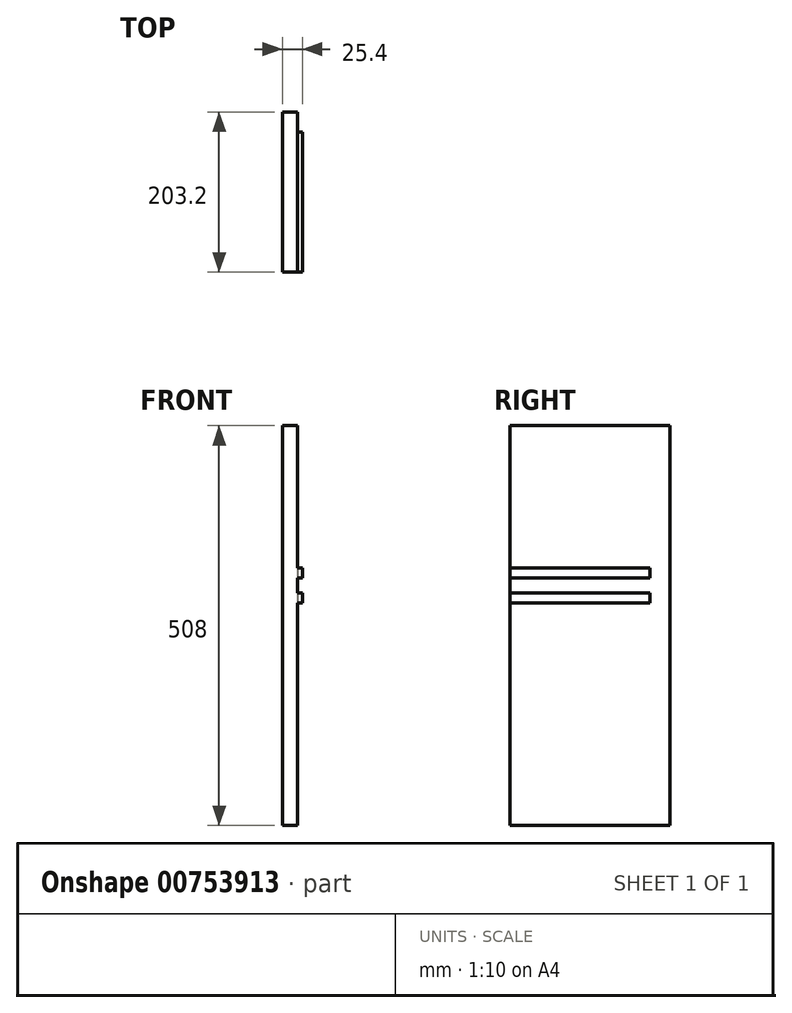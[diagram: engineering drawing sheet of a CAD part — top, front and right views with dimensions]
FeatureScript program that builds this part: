
annotation { "Feature Type Name" : "Feature", "Feature Type Description" : "" }
export const myFeature = defineFeature(function(context is Context, id is Id, definition is map)
    precondition{}
    {
        {
            var Q0;
            Q0=qCreatedBy(makeId("Right.planeOp"),FACE);
            var sketch = newSketch(context, id + "F0", { "sketchPlane" : qUnion([Q0])});
            skLineSegment(sketch, "E0.bottom", {"start": v(101.6, -254) * mm, "end": v(-101.6, -254) * mm});
            skLineSegment(sketch, "E0.top", {"start": v(101.6, 254) * mm, "end": v(-101.6, 254) * mm});
            skLineSegment(sketch, "E0.left", {"start": v(101.6, -254) * mm, "end": v(101.6, 254) * mm});
            skLineSegment(sketch, "E0.right", {"start": v(-101.6, -254) * mm, "end": v(-101.6, 254) * mm});
            skPoint(sketch, "E0.middle", {"position": v(0, 0) * mm});
            skSolve(sketch);
        }
        {
            var Q0;
            Q0=makeQuery(id+"F0.imprint","IMPRINT",FACE,{"disambiguationData":[TD([[makeQuery(id+"F0.imprint","IMPRINT",EDGE,{"derivedFrom":sQuery(id+"F0.wireOp",EDGE,"E0.bottom")}),-1.0]])]});
            extrude(context, id + "F1", {"entities" : qUnion([Q0]), "depth" : 19.05 * mm, "offsetDistance" : 25.4 * mm});
        }
        {
            var Q0;
            Q0=makeQuery(id+"F1.opExtrude","CAP_FACE",FACE,{"disambiguationData":[OSD([sQuery(id+"F0.wireOp",EDGE,"E0.bottom"),sQuery(id+"F0.wireOp",EDGE,"E0.top"),sQuery(id+"F0.wireOp",EDGE,"E0.left"),sQuery(id+"F0.wireOp",EDGE,"E0.right")])],"isStart":false});
            var sketch = newSketch(context, id + "F2", { "sketchPlane" : qUnion([Q0])});
            skLineSegment(sketch, "E1", {"start": v(0, 0) * mm, "end": v(0, 254) * mm});
            skLineSegment(sketch, "E2.bottom", {"start": v(-101.6, 73.02) * mm, "end": v(101.6, 73.02) * mm});
            skLineSegment(sketch, "E2.top", {"start": v(-101.6, 28.58) * mm, "end": v(101.6, 28.58) * mm});
            skLineSegment(sketch, "E2.left", {"start": v(-101.6, 73.02) * mm, "end": v(-101.6, 28.58) * mm});
            skLineSegment(sketch, "E2.right", {"start": v(101.6, 73.02) * mm, "end": v(101.6, 28.58) * mm});
            skPoint(sketch, "E2.middle", {"position": v(0, 50.8) * mm});
            skLineSegment(sketch, "E3.0", {"start": v(-101.72, 41.28) * mm, "end": v(101.6, 41.28) * mm});
            skLineSegment(sketch, "E4.0", {"start": v(-101.63, 60.32) * mm, "end": v(101.6, 60.32) * mm});
            skLineSegment(sketch, "E5", {"start": v(-101.72, 41.28) * mm, "end": v(-101.63, 60.32) * mm});
            skLineSegment(sketch, "E6.0", {"start": v(76.2, 73.02) * mm, "end": v(76.2, 27.98) * mm});
            skLineSegment(sketch, "E7", {"start": v(0, 50.8) * mm, "end": v(0, 254) * mm});
            skSolve(sketch);
        }
        {
            var Q0;
            {var subQ0=sQuery(id+"F2.wireOp",EDGE,"E6.0");var subQ1=sQuery(id+"F2.wireOp",EDGE,"E2.bottom");var subQ2=makeQuery(id+"F2.imprint","INTERSECT",VERTEX,{"derivedFrom":[subQ1,subQ0]});Q0=makeQuery(id+"F2.imprint","IMPRINT",FACE,{"disambiguationData":[TD([[makeQuery(id+"F2.imprint","IMPRINT",EDGE,{"disambiguationData":[TD([[subQ2,1.0]])],"derivedFrom":subQ1}),-1.0]])]});}
            var Q1;
            {var subQ0=sQuery(id+"F2.wireOp",EDGE,"E2.top");var subQ1=sQuery(id+"F2.wireOp",EDGE,"E1");var subQ2=makeQuery(id+"F2.imprint","INTERSECT",VERTEX,{"derivedFrom":[subQ1,subQ0]});Q1=makeQuery(id+"F2.imprint","IMPRINT",FACE,{"disambiguationData":[TD([[makeQuery(id+"F2.imprint","IMPRINT",EDGE,{"disambiguationData":[TD([[subQ2,-1.0]])],"derivedFrom":subQ1}),1.0]])]});}
            var Q2;
            {var subQ0=sQuery(id+"F2.wireOp",EDGE,"E2.top");var subQ1=sQuery(id+"F2.wireOp",EDGE,"E1");var subQ2=makeQuery(id+"F2.imprint","INTERSECT",VERTEX,{"derivedFrom":[subQ1,subQ0]});Q2=makeQuery(id+"F2.imprint","IMPRINT",FACE,{"disambiguationData":[TD([[makeQuery(id+"F2.imprint","IMPRINT",EDGE,{"disambiguationData":[TD([[subQ2,-1.0]])],"derivedFrom":subQ1}),-1.0]])]});}
            var Q3;
            {var subQ0=sQuery(id+"F2.wireOp",EDGE,"E2.left");var subQ5=sQuery(id+"F2.wireOp",EDGE,"E4.0");var subQ7=makeQuery(id+"F2.imprint","INTERSECT",VERTEX,{"derivedFrom":[subQ0,subQ5]});Q3=makeQuery(id+"F2.imprint","IMPRINT",FACE,{"disambiguationData":[TD([[makeQuery(id+"F2.imprint","IMPRINT",EDGE,{"disambiguationData":[TD([[subQ7,-1.0]])],"derivedFrom":subQ5}),1.0]])]});}
            extrude(context, id + "F3", {"entities" : qUnion([Q0, Q1, Q2, Q3]), "operationType" : NewBodyOperationType.ADD, "depth" : 6.35 * mm, "offsetDistance" : 25.4 * mm});
        }
    });
